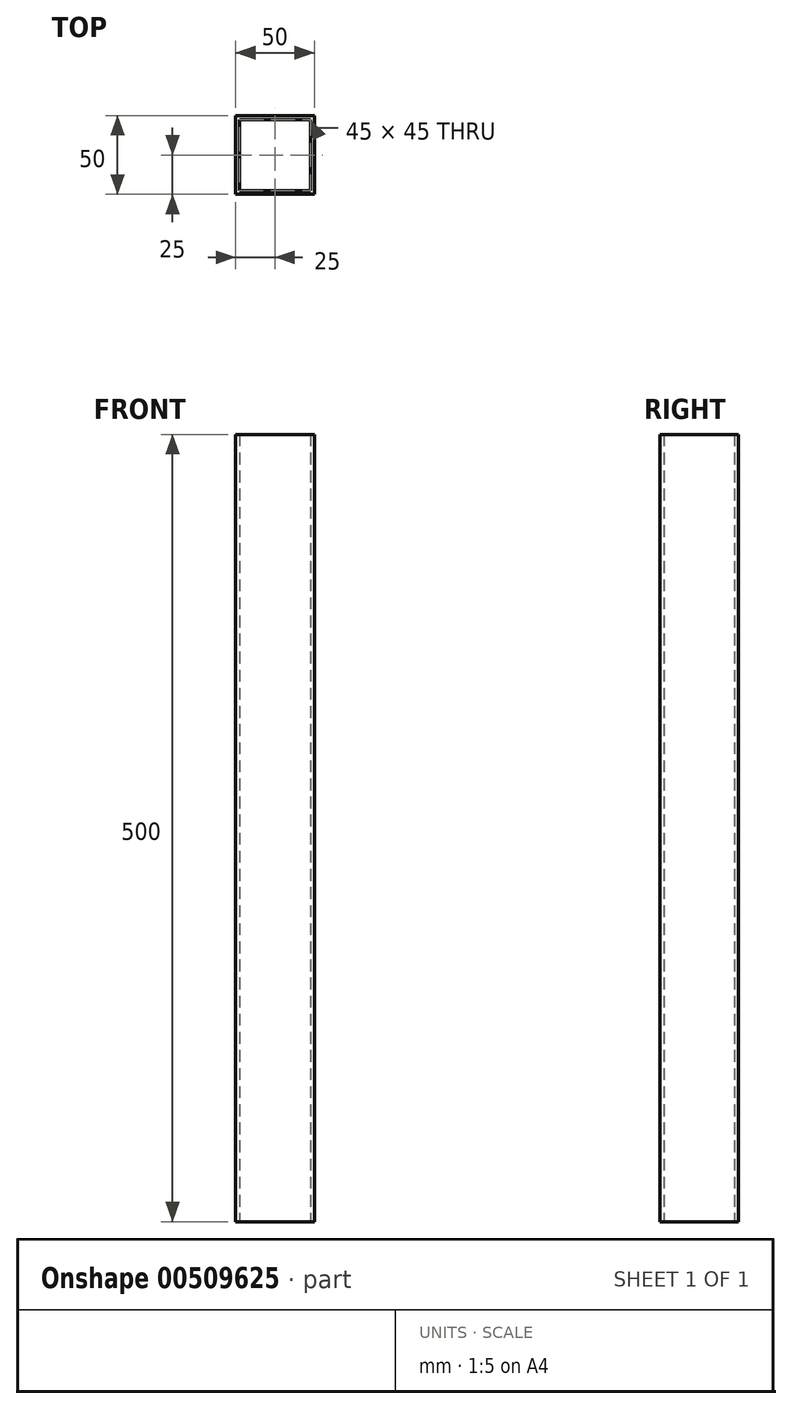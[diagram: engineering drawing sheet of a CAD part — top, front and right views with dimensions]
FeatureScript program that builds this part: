
annotation { "Feature Type Name" : "Feature", "Feature Type Description" : "" }
export const myFeature = defineFeature(function(context is Context, id is Id, definition is map)
    precondition{}
    {
        {
            var Q0;
            Q0=qCreatedBy(makeId("Top.planeOp"),FACE);
            var sketch = newSketch(context, id + "F0", { "sketchPlane" : qUnion([Q0])});
            skLineSegment(sketch, "E0.bottom", {"start": v(22.5, 22.5) * mm, "end": v(-22.5, 22.5) * mm});
            skLineSegment(sketch, "E0.top", {"start": v(22.5, -22.5) * mm, "end": v(-22.5, -22.5) * mm});
            skLineSegment(sketch, "E0.left", {"start": v(22.5, 22.5) * mm, "end": v(22.5, -22.5) * mm});
            skLineSegment(sketch, "E0.right", {"start": v(-22.5, 22.5) * mm, "end": v(-22.5, -22.5) * mm});
            skPoint(sketch, "E0.middle", {"position": v(0, 0) * mm});
            skLineSegment(sketch, "E1.bottom", {"start": v(25, 25) * mm, "end": v(-25, 25) * mm});
            skLineSegment(sketch, "E1.top", {"start": v(25, -25) * mm, "end": v(-25, -25) * mm});
            skLineSegment(sketch, "E1.left", {"start": v(25, 25) * mm, "end": v(25, -25) * mm});
            skLineSegment(sketch, "E1.right", {"start": v(-25, 25) * mm, "end": v(-25, -25) * mm});
            skSolve(sketch);
        }
        {
            var Q0;
            Q0=makeQuery(id+"F0.imprint","IMPRINT",FACE,{"disambiguationData":[TD([[makeQuery(id+"F0.imprint","IMPRINT",EDGE,{"derivedFrom":sQuery(id+"F0.wireOp",EDGE,"E0.bottom")}),-1.0]])]});
            extrude(context, id + "F1", {"entities" : qUnion([Q0]), "depth" : 500 * mm});
        }
    });
